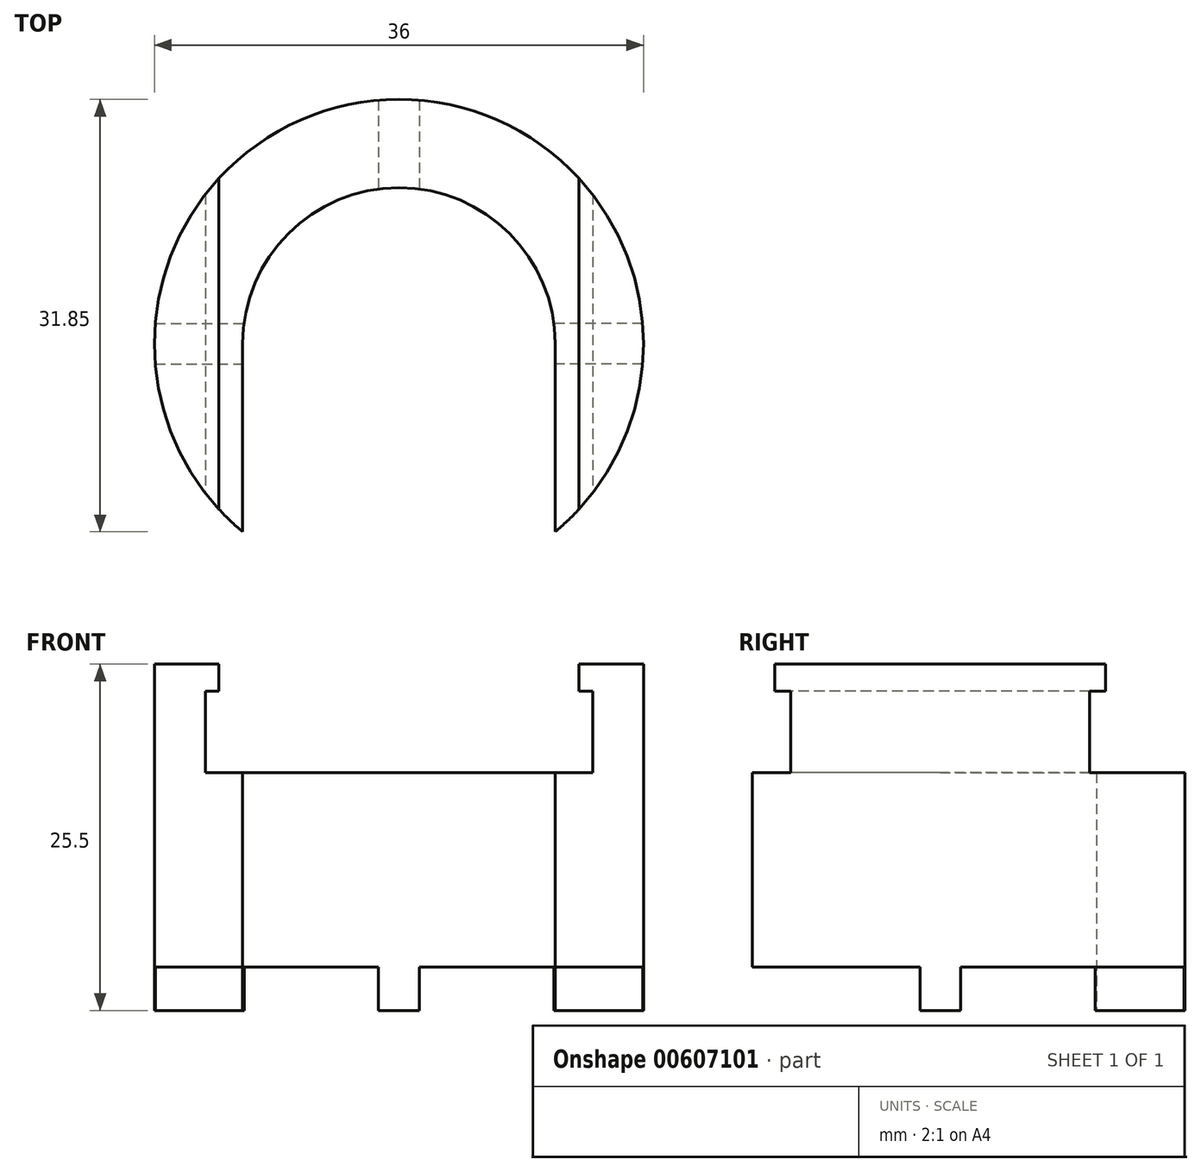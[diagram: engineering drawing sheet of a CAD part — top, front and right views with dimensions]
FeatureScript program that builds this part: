
annotation { "Feature Type Name" : "Feature", "Feature Type Description" : "" }
export const myFeature = defineFeature(function(context is Context, id is Id, definition is map)
    precondition{}
    {
        {
            var Q0;
            Q0=qCreatedBy(makeId("Top.planeOp"),FACE);
            var sketch = newSketch(context, id + "F0", { "sketchPlane" : qUnion([Q0])});
            skArc(sketch, "E0", {"start": v(11.5, -13.85) * mm, "mid": v(0, 18) * mm, "end": v(-11.5, -13.85) * mm});
            skArc(sketch, "E1", {"start": v(11.5, 0) * mm, "mid": v(0, 11.5) * mm, "end": v(-11.5, 0) * mm});
            skLineSegment(sketch, "E2", {"start": v(-11.5, 0) * mm, "end": v(-11.5, -13.85) * mm});
            skLineSegment(sketch, "E3", {"start": v(11.5, 0) * mm, "end": v(11.5, -13.85) * mm});
            skSolve(sketch);
        }
        {
            var Q0;
            Q0 = qSketchRegion(id + "F0", true);
            extrude(context, id + "F1", {"entities" : qUnion([Q0]), "depth" : 25.5 * mm, "offsetDistance" : 25 * mm});
        }
        {
            var Q0;
            Q0=qCreatedBy(makeId("Front.planeOp"),FACE);
            var sketch = newSketch(context, id + "F2", { "sketchPlane" : qUnion([Q0])});
            skLineSegment(sketch, "E4.bottom", {"start": v(-14.25, 23.5) * mm, "end": v(14.25, 23.5) * mm});
            skLineSegment(sketch, "E4.top", {"start": v(-14.25, 17.5) * mm, "end": v(14.25, 17.5) * mm});
            skLineSegment(sketch, "E4.left", {"start": v(-14.25, 23.5) * mm, "end": v(-14.25, 17.5) * mm});
            skLineSegment(sketch, "E4.right", {"start": v(14.25, 23.5) * mm, "end": v(14.25, 17.5) * mm});
            skLineSegment(sketch, "E5", {"start": v(0, 0) * mm, "end": v(0, 37.1) * mm, "construction": true});
            skLineSegment(sketch, "E6", {"start": v(-13.25, 23.5) * mm, "end": v(-13.25, 25.5) * mm});
            skLineSegment(sketch, "E7", {"start": v(-13.25, 25.5) * mm, "end": v(13.25, 25.5) * mm});
            skLineSegment(sketch, "E8", {"start": v(13.25, 25.5) * mm, "end": v(13.25, 23.5) * mm});
            skSolve(sketch);
        }
        {
            var Q0;
            Q0 = qSketchRegion(id + "F2", true);
            extrude(context, id + "F3", {"entities" : qUnion([Q0]), "operationType" : NewBodyOperationType.REMOVE, "endBound" : BoundingType.THROUGH_ALL, "oppositeDirection" : true, "depth" : 25 * mm, "offsetDistance" : 25 * mm});
        }
        {
            var Q0;
            Q0 = qSketchRegion(id + "F2", true);
            extrude(context, id + "F4", {"entities" : qUnion([Q0]), "operationType" : NewBodyOperationType.REMOVE, "endBound" : BoundingType.THROUGH_ALL, "depth" : 25 * mm, "offsetDistance" : 25 * mm});
        }
        {
            var Q0;
            Q0=makeQuery(id+"F1.opExtrude","CAP_FACE",FACE,{"disambiguationData":[OSD([sQuery(id+"F0.wireOp",EDGE,"E0"),sQuery(id+"F0.wireOp",EDGE,"E1"),sQuery(id+"F0.wireOp",EDGE,"E2"),sQuery(id+"F0.wireOp",EDGE,"E3")])],"isStart":true});
            var sketch = newSketch(context, id + "F5", { "sketchPlane" : qUnion([Q0])});
            skLineSegment(sketch, "E9", {"start": v(-1.5, -17.94) * mm, "end": v(-1.5, -11.4) * mm});
            skArc(sketch, "E10.0", {"start": v(11.5, 0) * mm, "mid": v(0, -11.5) * mm, "end": v(-11.5, 0) * mm});
            skLineSegment(sketch, "E11", {"start": v(0, 0) * mm, "end": v(0, 9.82) * mm, "construction": true});
            skLineSegment(sketch, "E12.MirrorCS", {"start": v(1.5, -17.94) * mm, "end": v(1.5, -11.4) * mm});
            skArc(sketch, "E13.0", {"start": v(11.5, 13.85) * mm, "mid": v(0, -18) * mm, "end": v(-11.5, 13.85) * mm});
            skLineSegment(sketch, "E14", {"start": v(0, 0) * mm, "end": v(7.01, 0) * mm, "construction": true});
            skLineSegment(sketch, "E15", {"start": v(-17.94, 1.5) * mm, "end": v(-11.5, 1.5) * mm});
            skLineSegment(sketch, "E16.MirrorCS", {"start": v(-17.94, -1.5) * mm, "end": v(-11.4, -1.5) * mm});
            skLineSegment(sketch, "E17.0", {"start": v(-11.5, 0) * mm, "end": v(-11.5, 13.85) * mm});
            skLineSegment(sketch, "E17.1", {"start": v(11.5, 0) * mm, "end": v(11.5, 13.85) * mm});
            skPoint(sketch, "E18.orphan", {"position": v(-6.45, 1.5) * mm});
            skPoint(sketch, "E19.orphan", {"position": v(-6.45, -1.5) * mm});
            skPoint(sketch, "E20.orphan", {"position": v(-20.39, -1.5) * mm});
            skPoint(sketch, "E21.orphan", {"position": v(-20.39, 1.5) * mm});
            skPoint(sketch, "E22.orphan", {"position": v(-1.5, -8.05) * mm});
            skPoint(sketch, "E23.orphan", {"position": v(1.5, -8.05) * mm});
            skPoint(sketch, "E24.MirrorP", {"position": v(6.45, -1.5) * mm});
            skPoint(sketch, "E25.MirrorP", {"position": v(6.45, 1.5) * mm});
            skLineSegment(sketch, "E26.MirrorCS", {"start": v(17.94, -1.5) * mm, "end": v(11.4, -1.5) * mm});
            skPoint(sketch, "E27.MirrorP", {"position": v(20.39, -1.5) * mm});
            skLineSegment(sketch, "E28.MirrorCS", {"start": v(17.94, 1.5) * mm, "end": v(11.5, 1.5) * mm});
            skPoint(sketch, "E29.MirrorP", {"position": v(20.39, 1.5) * mm});
            skSolve(sketch);
        }
        {
            var Q0;
            {var subQ3=sQuery(id+"F5.wireOp",EDGE,"E15");Q0=makeQuery(id+"F5.imprint","IMPRINT",FACE,{"disambiguationData":[TD([[makeQuery(id+"F5.imprint","IMPRINT",EDGE,{"derivedFrom":subQ3}),1.0]])]});}
            var Q1;
            {var subQ0=sQuery(id+"F5.wireOp",EDGE,"E9");Q1=makeQuery(id+"F5.imprint","IMPRINT",FACE,{"disambiguationData":[TD([[makeQuery(id+"F5.imprint","IMPRINT",EDGE,{"derivedFrom":subQ0}),1.0]])]});}
            var Q2;
            {var subQ0=sQuery(id+"F5.wireOp",EDGE,"E12.MirrorCS");Q2=makeQuery(id+"F5.imprint","IMPRINT",FACE,{"disambiguationData":[TD([[makeQuery(id+"F5.imprint","IMPRINT",EDGE,{"derivedFrom":subQ0}),-1.0]])]});}
            var Q3;
            {var subQ3=sQuery(id+"F5.wireOp",EDGE,"E28.MirrorCS");Q3=makeQuery(id+"F5.imprint","IMPRINT",FACE,{"disambiguationData":[TD([[makeQuery(id+"F5.imprint","IMPRINT",EDGE,{"derivedFrom":subQ3}),-1.0]])]});}
            extrude(context, id + "F6", {"entities" : qUnion([Q0, Q1, Q2, Q3]), "operationType" : NewBodyOperationType.REMOVE, "oppositeDirection" : true, "depth" : 3.2 * mm, "offsetDistance" : 25 * mm});
        }
    });
